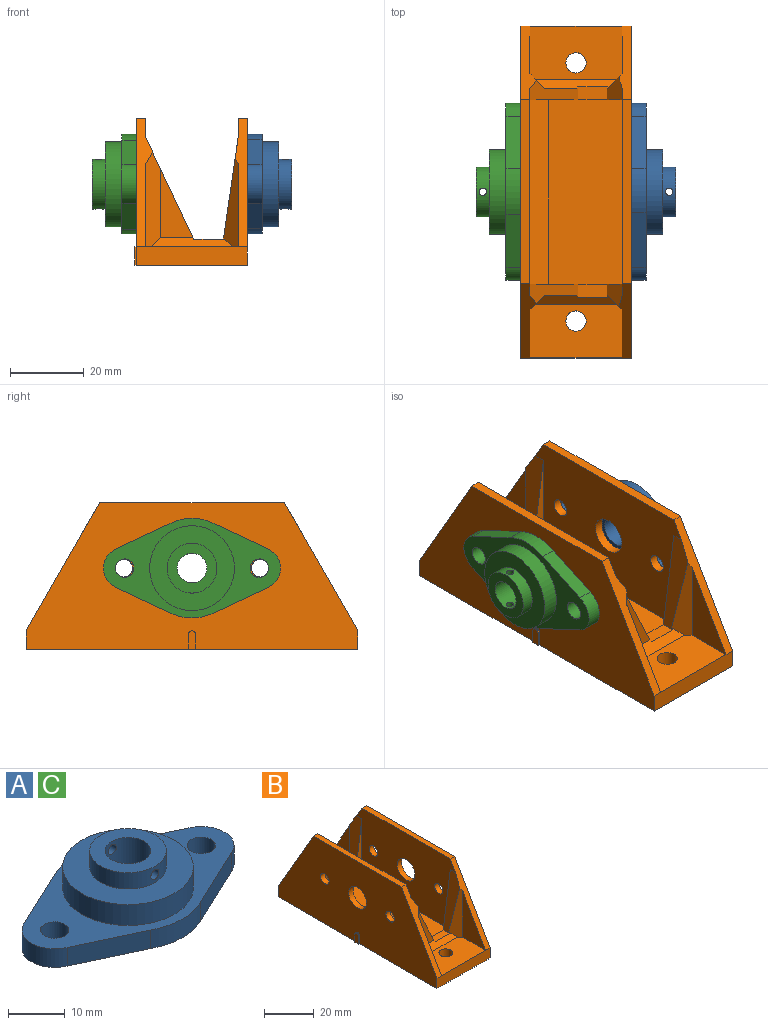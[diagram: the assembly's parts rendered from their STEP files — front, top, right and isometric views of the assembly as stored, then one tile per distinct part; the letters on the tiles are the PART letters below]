
ASSEMBLY  parts=3 mates=2
PART A: 19 faces, bbox 48x27x12 mm
  f0: cylinder r=6.75mm len=13.5mm, axis (0,0,-1), area 142.1mm2, adj f15,f16,f17,f18
  f1: cylinder r=4.01mm len=12mm, axis (0,0,1), area 296mm2, adj f13,f16,f17,f18
  f2: cylinder r=13.5mm len=12.55mm, axis (0,0,-1), area 52.2mm2, adj f3,f10,f12,f13
  f3: plane 14.17x6.64mm, normal (-0.42,0.91,0), area 62.6mm2, adj f2,f4,f12,f13
  f4: cylinder r=5.75mm len=10.62mm, axis (0,0,-1), area 54.2mm2, adj f3,f5,f12,f13
  f5: plane 14.17x6.64mm, normal (-0.42,-0.91,0), area 62.6mm2, adj f4,f6,f12,f13
  f6: cylinder r=13.5mm len=12mm, axis (0,0,-1), area 49.8mm2, adj f5,f7,f12,f13
  f7: plane 14.72x6.91mm, normal (0.42,-0.91,0), area 65.1mm2, adj f6,f8,f12,f13
  f8: cylinder r=5.75mm len=10.62mm, axis (0,0,-1), area 54.2mm2, adj f7,f10,f12,f13
  f9: cylinder r=2.5mm len=5mm, axis (0,0,-1), area 62.8mm2, adj f12,f13
  f10: plane 14.17x6.64mm, normal (0.42,0.91,0), area 62.6mm2, adj f2,f8,f12,f13
  f11: cylinder r=2.5mm len=5mm, axis (0,0,-1), area 62.8mm2, adj f12,f13
  f12: plane 48x27mm, normal (0,0,1), area 415.6mm2, adj f2,f3,f4,f5,f6,f7,f8,f9
  f13: plane 48x27mm, normal (0,0,-1), area 780.5mm2, adj f1,f2,f3,f4,f5,f6,f7,f8
  f14: cylinder r=11.5mm len=23mm, axis (0,0,-1), area 325.2mm2, adj f12,f15
  f15: plane 23x23mm, normal (0,0,1), area 272.3mm2, adj f0,f14
  f16: plane 13.5x13.5mm, normal (0,0,1), area 92.6mm2, adj f0,f1
  f17: cylinder r=1mm len=2.87mm, axis (0,-1,0), area 17.4mm2, adj f0,f1
  f18: cylinder r=1mm len=2.87mm, axis (0,-1,0), area 17.4mm2, adj f0,f1
PART B: 49 faces, bbox 30.5x90x39.8 mm
  f0: plane 90x39.75mm, normal (-1,0,0), area 2758.2mm2, adj f2,f3,f13,f21,f22,f24,f25,f28
  f1: plane 18.56x8.76mm, normal (0,-1,0), area 81.3mm2, adj f35,f39,f44
  f2: plane 34.75x20mm, normal (0,0.87,0.5), area 107.5mm2, adj f0,f9,f13,f17,f24,f34,f43
  f3: plane 34.75x20mm, normal (0,-0.87,0.5), area 107.5mm2, adj f0,f9,f11,f13,f25,f35,f44
  f4: plane 18.56x8.76mm, normal (0,1,0), area 81.3mm2, adj f34,f38,f43
  f5: plane 29.54x25mm, normal (0,1,0), area 271.6mm2, adj f9,f10,f12,f35,f36,f37,f40
  f6: plane 29.54x25mm, normal (0,-1,0), area 271.6mm2, adj f9,f10,f12,f32,f33,f34,f40
  f7: plane 25x14.5mm, normal (0,0,1), area 336.5mm2, adj f8,f17,f24,f27,f38,f41,f43
  f8: plane 22.59x13mm, normal (-1,0,0), area 146.8mm2, adj f7,f14,f41
  f9: plane 56x29.75mm, normal (1,0,0), area 1388.4mm2, adj f2,f3,f5,f6,f13,f22,f28,f29
  f10: plane 50x20mm, normal (0,0,1), area 1000mm2, adj f5,f6,f12,f40
  f11: plane 22.59x13mm, normal (1,0,0), area 146.8mm2, adj f3,f19,f44
  f12: plane 56x34.75mm, normal (-1,0,0), area 1638.4mm2, adj f5,f6,f10,f14,f15,f16,f23,f30
  f13: plane 50x2.5mm, normal (0,0,1), area 125mm2, adj f0,f2,f3,f9
  f14: plane 34.75x20mm, normal (0,0.87,0.5), area 103.5mm2, adj f8,f12,f15,f20,f24,f32,f41
  f15: plane 50x2.5mm, normal (0,0,1), area 125mm2, adj f12,f14,f16,f20
  f16: plane 34.75x20mm, normal (0,-0.87,0.5), area 103.5mm2, adj f12,f15,f18,f20,f25,f37,f42
  f17: plane 22.59x13mm, normal (1,0,0), area 146.8mm2, adj f2,f7,f43
  f18: plane 22.59x13mm, normal (-1,0,0), area 146.8mm2, adj f16,f19,f42
  f19: plane 25x14.5mm, normal (0,0,1), area 336.5mm2, adj f11,f18,f25,f26,f39,f42,f44
  f20: plane 90x39.75mm, normal (1,0,0), area 2767.8mm2, adj f14,f15,f16,f21,f23,f24,f25,f30
  f21: plane 90x30.5mm, normal (0,0,-1), area 2653.5mm2, adj f0,f20,f24,f25,f26,f27,f45,f46
  f22: cylinder r=5mm len=10mm, axis (1,0,0), area 78.5mm2, adj f0,f9
  f23: cylinder r=5mm len=10mm, axis (1,0,0), area 78.5mm2, adj f12,f20
  f24: plane 30x5mm, normal (0,1,0), area 150mm2, adj f0,f2,f7,f14,f20,f21
  f25: plane 30x5mm, normal (0,-1,0), area 150mm2, adj f0,f3,f16,f19,f20,f21
  f26: cylinder r=2.75mm len=5.5mm, axis (0,0,1), area 86.4mm2, adj f19,f21
  f27: cylinder r=2.75mm len=5.5mm, axis (0,0,1), area 86.4mm2, adj f7,f21
  f28: cylinder r=2.4mm len=4.8mm, axis (1,0,0), area 37.7mm2, adj f0,f9
  f29: cylinder r=2.4mm len=4.8mm, axis (1,0,0), area 37.7mm2, adj f0,f9
  f30: cylinder r=2.4mm len=4.8mm, axis (1,0,0), area 37.7mm2, adj f12,f20
  f31: cylinder r=2.4mm len=4.8mm, axis (1,0,0), area 37.7mm2, adj f12,f20
  f32: plane 27.54x6.19mm, normal (-0.99,0,0.14), area 128mm2, adj f6,f12,f14,f33,f38,f41
  f33: plane 8x3.5mm, normal (0,0,1), area 28mm2, adj f6,f32,f34,f38
  f34: plane 27.54x13mm, normal (0.9,0,0.43), area 101.8mm2, adj f2,f4,f6,f9,f33,f38,f43
  f35: plane 27.54x13mm, normal (0.9,0,0.43), area 101.8mm2, adj f1,f3,f5,f9,f36,f39,f44
  f36: plane 8x3.5mm, normal (0,0,1), area 28mm2, adj f5,f35,f37,f39
  f37: plane 27.54x6.19mm, normal (-0.99,0,0.14), area 128mm2, adj f5,f12,f16,f36,f39,f42
  f38: plane 22x2.5mm, normal (0,0.71,0.71), area 63.2mm2, adj f4,f7,f32,f33,f34,f41,f43
  f39: plane 22x2.5mm, normal (0,-0.71,0.71), area 63.2mm2, adj f1,f19,f35,f36,f37,f42,f44
  f40: plane 50x5mm, normal (0.71,0,0.71), area 353.6mm2, adj f5,f6,f9,f10
  f41: plane 23.99x3.94mm, normal (-0.71,0.71,0), area 80.8mm2, adj f7,f8,f14,f32,f38
  f42: plane 23.99x3.94mm, normal (-0.71,-0.71,0), area 80.8mm2, adj f16,f18,f19,f37,f39
  f43: plane 25.72x4mm, normal (0.71,0.71,0), area 129.8mm2, adj f2,f4,f7,f17,f34,f38
  f44: plane 25.72x4mm, normal (0.71,-0.71,0), area 129.8mm2, adj f1,f3,f11,f19,f35,f39
  f45: plane 4x0.5mm, normal (0,1,0), area 2mm2, adj f0,f21,f47,f48
  f46: plane 4x0.5mm, normal (0,-1,0), area 2mm2, adj f0,f21,f47,f48
  f47: plane 5x2mm, normal (-1,0,0), area 9.6mm2, adj f21,f45,f46,f48
  f48: cylinder r=1mm len=2mm, axis (1,0,0), area 1.6mm2, adj f0,f45,f46,f47
PART C: same geometry as A
PLACE A rot(axis=(-0.58,0.58,-0.58),120deg) t=(8.76,14.49,29.48)mm
PLACE B t=(-6.24,14.49,7.48)mm
PLACE C rot(axis=(0.58,-0.58,-0.58),120deg) t=(-21.24,14.49,29.48)mm
MATE fastened C.f6 <-> B.f22  axis (1,0,0) through (-21.24,14.49,29.48)mm
MATE fastened A.f6 <-> B.f22  axis (-1,0,0) through (8.76,14.49,29.48)mm
